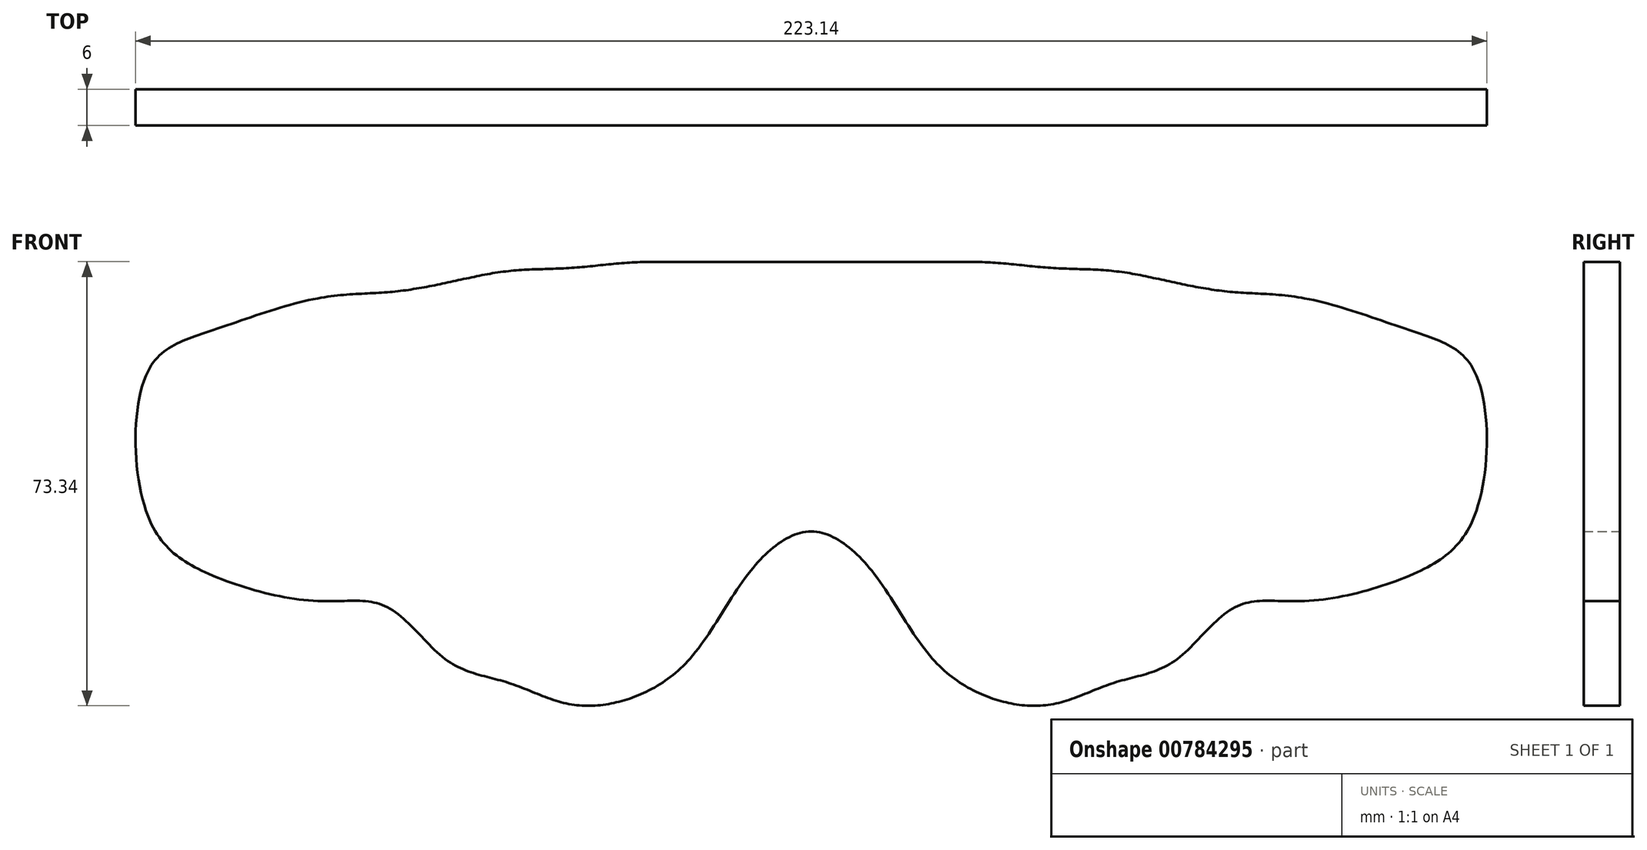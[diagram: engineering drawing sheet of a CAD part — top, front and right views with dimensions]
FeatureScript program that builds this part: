
annotation { "Feature Type Name" : "Feature", "Feature Type Description" : "" }
export const myFeature = defineFeature(function(context is Context, id is Id, definition is map)
    precondition{}
    {
        {
            var Q0;
            Q0=qCreatedBy(makeId("Front.planeOp"),FACE);
            var sketch = newSketch(context, id + "F0", { "sketchPlane" : qUnion([Q0])});
            skLineSegment(sketch, "E0", {"start": v(0, 14.75) * mm, "end": v(0, -14.75) * mm, "construction": true});
            skLineSegment(sketch, "E1", {"start": v(-99.04, 14.75) * mm, "end": v(102.18, 14.75) * mm, "construction": true});
            skLineSegment(sketch, "E2", {"start": v(-10, 14.75) * mm, "end": v(-10, -21.25) * mm, "construction": true});
            skLineSegment(sketch, "E3", {"start": v(-20, 14.75) * mm, "end": v(-20, -34.75) * mm, "construction": true});
            skLineSegment(sketch, "E4", {"start": v(-30, 14.65) * mm, "end": v(-30, -41.35) * mm, "construction": true});
            skLineSegment(sketch, "E5", {"start": v(-40, 14.25) * mm, "end": v(-40, -41.25) * mm, "construction": true});
            skLineSegment(sketch, "E6", {"start": v(-50, 13.25) * mm, "end": v(-50, -38.75) * mm, "construction": true});
            skFitSpline(sketch, "E7", {"points": [v(0, 14.75) * mm, v(-10, 14.75) * mm, v(-20, 14.75) * mm, v(-30, 14.65) * mm, v(-40, 14.25) * mm, v(-50, 13.25) * mm, v(-70, 6.75) * mm, v(-81.5, -9.25) * mm, v(-70, -29.25) * mm, v(-50, -38.75) * mm, v(-40, -41.25) * mm, v(-30, -41.35) * mm, v(-20, -34.75) * mm, v(-10, -21.25) * mm, v(0, -14.75) * mm], "startDerivative": vector(-114.45, 0) * mm, "endDerivative": vector(302.04, 11.48) * mm});
            skFitSpline(sketch, "E8.MirrorCS", {"points": [v(0, 14.75) * mm, v(10, 14.75) * mm, v(20, 14.75) * mm, v(30, 14.65) * mm, v(40, 14.25) * mm, v(50, 13.25) * mm, v(70, 6.75) * mm, v(81.5, -9.25) * mm, v(70, -29.25) * mm, v(50, -38.75) * mm, v(40, -41.25) * mm, v(30, -41.35) * mm, v(20, -34.75) * mm, v(10, -21.25) * mm, v(0, -14.75) * mm], "startDerivative": vector(114.45, 0) * mm, "endDerivative": vector(-302.04, 11.48) * mm});
            skLineSegment(sketch, "E9", {"start": v(-70, 6.75) * mm, "end": v(-70, -29.25) * mm, "construction": true});
            skPoint(sketch, "E10", {"position": v(0, 0) * mm});
            skLineSegment(sketch, "E11", {"start": v(-60, 11.04) * mm, "end": v(-60, -35.14) * mm, "construction": true});
            skSolve(sketch);
        }
        {
            var Q0;
            Q0=makeQuery(id+"F0.imprint","IMPRINT",FACE,{"disambiguationData":[TD([[makeQuery(id+"F0.imprint","IMPRINT",EDGE,{"derivedFrom":sQuery(id+"F0.wireOp",EDGE,"E7")}),1.0]])]});
            extrude(context, id + "F1", {"entities" : qUnion([Q0]), "depth" : .6 * mm, "offsetDistance" : 25 * mm});
        }
        {
            var Q0;
            Q0=qCreatedBy(makeId("Front.planeOp"),FACE);
            var sketch = newSketch(context, id + "F2", { "sketchPlane" : qUnion([Q0])});
            skLineSegment(sketch, "E12", {"start": v(0, 20.75) * mm, "end": v(0, -23.75) * mm});
            skLineSegment(sketch, "E13", {"start": v(-10, 20.75) * mm, "end": v(-10, -30.25) * mm});
            skLineSegment(sketch, "E14", {"start": v(-20, 20.75) * mm, "end": v(-20, -44.75) * mm});
            skLineSegment(sketch, "E15", {"start": v(-30, 20.65) * mm, "end": v(-30, -51.35) * mm});
            skLineSegment(sketch, "E16", {"start": v(-40, 19.75) * mm, "end": v(-40, -52.25) * mm});
            skLineSegment(sketch, "E17", {"start": v(-50, -48.75) * mm, "end": v(-50, 19.25) * mm});
            skLineSegment(sketch, "E18", {"start": v(-60, 17.36) * mm, "end": v(-60, -45.14) * mm});
            skLineSegment(sketch, "E19", {"start": v(-70, 15.75) * mm, "end": v(-70, -36.25) * mm});
            skLineSegment(sketch, "E20", {"start": v(-81.5, 14.75) * mm, "end": v(-81.5, -35.25) * mm});
            skLineSegment(sketch, "E21", {"start": v(-99.5, 9.25) * mm, "end": v(-99.5, -30.75) * mm});
            skPoint(sketch, "E22", {"position": v(-109.5, -9.25) * mm});
            skLineSegment(sketch, "E23", {"start": v(-109.5, -21.25) * mm, "end": v(-109.5, 2.75) * mm});
            skLineSegment(sketch, "E24.MirrorCS", {"start": v(10, 20.75) * mm, "end": v(10, -30.25) * mm});
            skLineSegment(sketch, "E25.MirrorCS", {"start": v(20, 20.75) * mm, "end": v(20, -44.75) * mm});
            skLineSegment(sketch, "E26.MirrorCS", {"start": v(30, 20.65) * mm, "end": v(30, -51.35) * mm});
            skLineSegment(sketch, "E27.MirrorCS", {"start": v(40, 19.75) * mm, "end": v(40, -52.25) * mm});
            skLineSegment(sketch, "E28.MirrorCS", {"start": v(50, -48.75) * mm, "end": v(50, 19.25) * mm});
            skLineSegment(sketch, "E29.MirrorCS", {"start": v(60, 17.36) * mm, "end": v(60, -45.14) * mm});
            skLineSegment(sketch, "E30.MirrorCS", {"start": v(70, 15.75) * mm, "end": v(70, -36.25) * mm});
            skLineSegment(sketch, "E31.MirrorCS", {"start": v(81.5, 14.75) * mm, "end": v(81.5, -35.25) * mm});
            skLineSegment(sketch, "E32.MirrorCS", {"start": v(99.5, 9.25) * mm, "end": v(99.5, -30.75) * mm});
            skLineSegment(sketch, "E33.MirrorCS", {"start": v(109.5, -21.25) * mm, "end": v(109.5, 2.75) * mm});
            skFitSpline(sketch, "E34", {"points": [v(0, 20.75) * mm, v(-10, 20.75) * mm, v(-20, 20.75) * mm, v(-30, 20.65) * mm, v(-40, 19.75) * mm, v(-50, 19.25) * mm, v(-60, 17.36) * mm, v(-70, 15.75) * mm, v(-81.5, 14.75) * mm, v(-99.5, 9.25) * mm, v(-109.5, 2.75) * mm, v(-109.5, -21.25) * mm, v(-99.5, -30.75) * mm, v(-81.5, -35.25) * mm, v(-70, -36.25) * mm, v(-60, -45.14) * mm, v(-50, -48.75) * mm, v(-40, -52.25) * mm, v(-30, -51.35) * mm, v(-20, -44.75) * mm, v(-10, -30.25) * mm, v(0, -23.75) * mm, v(10, -30.25) * mm, v(20, -44.75) * mm, v(30, -51.35) * mm, v(40, -52.25) * mm, v(50, -48.75) * mm, v(60, -45.14) * mm, v(70, -36.25) * mm, v(81.5, -35.25) * mm, v(99.5, -30.75) * mm, v(109.5, -21.25) * mm, v(109.5, 2.75) * mm, v(99.5, 9.25) * mm, v(81.5, 14.75) * mm, v(70, 15.75) * mm, v(60, 17.36) * mm, v(50, 19.25) * mm, v(40, 19.75) * mm, v(30, 20.65) * mm, v(20, 20.75) * mm, v(10, 20.75) * mm, v(0, 20.75) * mm]});
            skSolve(sketch);
        }
        {
            var Q0;
            Q0 = qSketchRegion(id + "F2", true);
            var Q1;
            Q1=makeQuery(id+"F1.opExtrude","CAP_FACE",FACE,{"disambiguationData":[OSD([sQuery(id+"F0.wireOp",EDGE,"E7"),sQuery(id+"F0.wireOp",EDGE,"E8.MirrorCS")])],"isStart":true});
            extrude(context, id + "F3", {"entities" : qUnion([Q0]), "operationType" : NewBodyOperationType.ADD, "depth" : 6 * mm, "endBoundEntityFace" : qUnion([Q1]), "offsetDistance" : 25 * mm});
        }
    });
